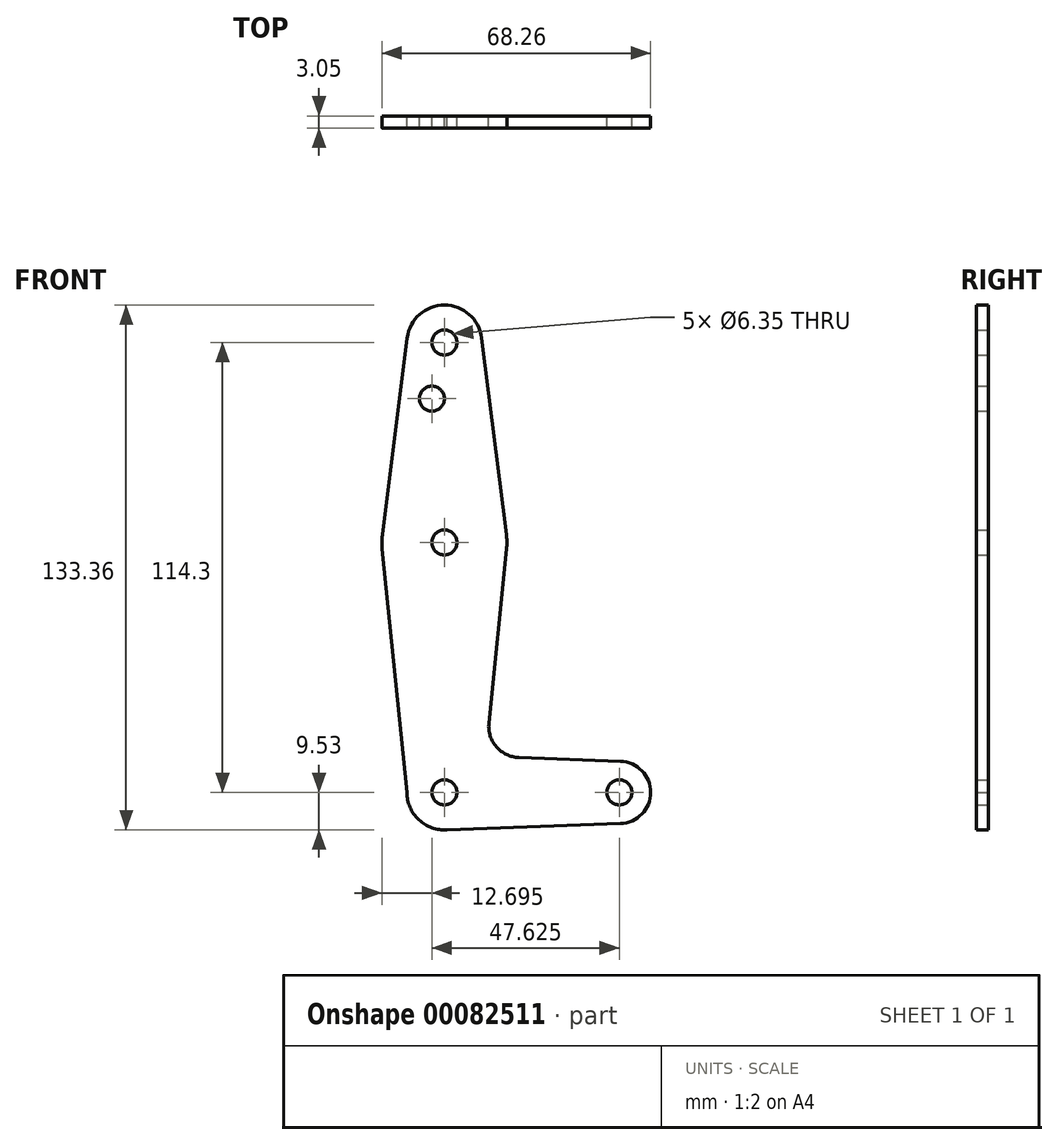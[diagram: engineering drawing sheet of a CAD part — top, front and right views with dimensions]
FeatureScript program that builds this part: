
annotation { "Feature Type Name" : "Feature", "Feature Type Description" : "" }
export const myFeature = defineFeature(function(context is Context, id is Id, definition is map)
    precondition{}
    {
        {
            var Q0;
            Q0=qCreatedBy(makeId("Front.planeOp"),FACE);
            var sketch = newSketch(context, id + "F0", { "sketchPlane" : qUnion([Q0])});
            skCircle(sketch, "E0", {"center": v(0, 114.3) * mm, "radius": 9.53 * mm});
            skCircle(sketch, "E1", {"center": v(0, 63.5) * mm, "radius": 15.88 * mm});
            skCircle(sketch, "E2", {"center": v(0, 0) * mm, "radius": 9.53 * mm});
            skCircle(sketch, "E3", {"center": v(44.45, 0) * mm, "radius": 7.94 * mm});
            skLineSegment(sketch, "E4", {"start": v(0, 114.3) * mm, "end": v(0, 63.5) * mm, "construction": true});
            skLineSegment(sketch, "E5", {"start": v(0, 63.5) * mm, "end": v(0, 0) * mm, "construction": true});
            skLineSegment(sketch, "E6", {"start": v(0, 0) * mm, "end": v(44.45, 0) * mm, "construction": true});
            skLineSegment(sketch, "E7", {"start": v(-9.45, 115.5) * mm, "end": v(-15.75, 65.48) * mm});
            skLineSegment(sketch, "E8", {"start": v(9.45, 115.5) * mm, "end": v(15.75, 65.48) * mm});
            skLineSegment(sketch, "E9", {"start": v(-9.53, 0) * mm, "end": v(-15.8, 61.9) * mm});
            skLineSegment(sketch, "E10", {"start": v(0, -9.52) * mm, "end": v(44.73, -7.93) * mm});
            skCircle(sketch, "E11", {"center": v(0, 114.3) * mm, "radius": 3.17 * mm});
            skCircle(sketch, "E12", {"center": v(-3.17, 100.03) * mm, "radius": 3.17 * mm});
            skCircle(sketch, "E13", {"center": v(0, 63.5) * mm, "radius": 3.17 * mm});
            skCircle(sketch, "E14", {"center": v(0, 0) * mm, "radius": 3.17 * mm});
            skCircle(sketch, "E15", {"center": v(44.45, 0) * mm, "radius": 3.17 * mm});
            skLineSegment(sketch, "E16", {"start": v(11.3, 17.6) * mm, "end": v(15.8, 61.9) * mm});
            skLineSegment(sketch, "E17", {"start": v(18.93, 8.85) * mm, "end": v(44.73, 7.93) * mm});
            skArc(sketch, "E18.filletArc", {"start": v(11.3, 17.6) * mm, "mid": v(13.22, 11.57) * mm, "end": v(18.93, 8.85) * mm});
            skSolve(sketch);
        }
        {
            var Q0;
            Q0 = qSketchRegion(id + "F0", true);
            extrude(context, id + "F1", {"entities" : qUnion([Q0]), "depth" : 3.05 * mm});
        }
    });
